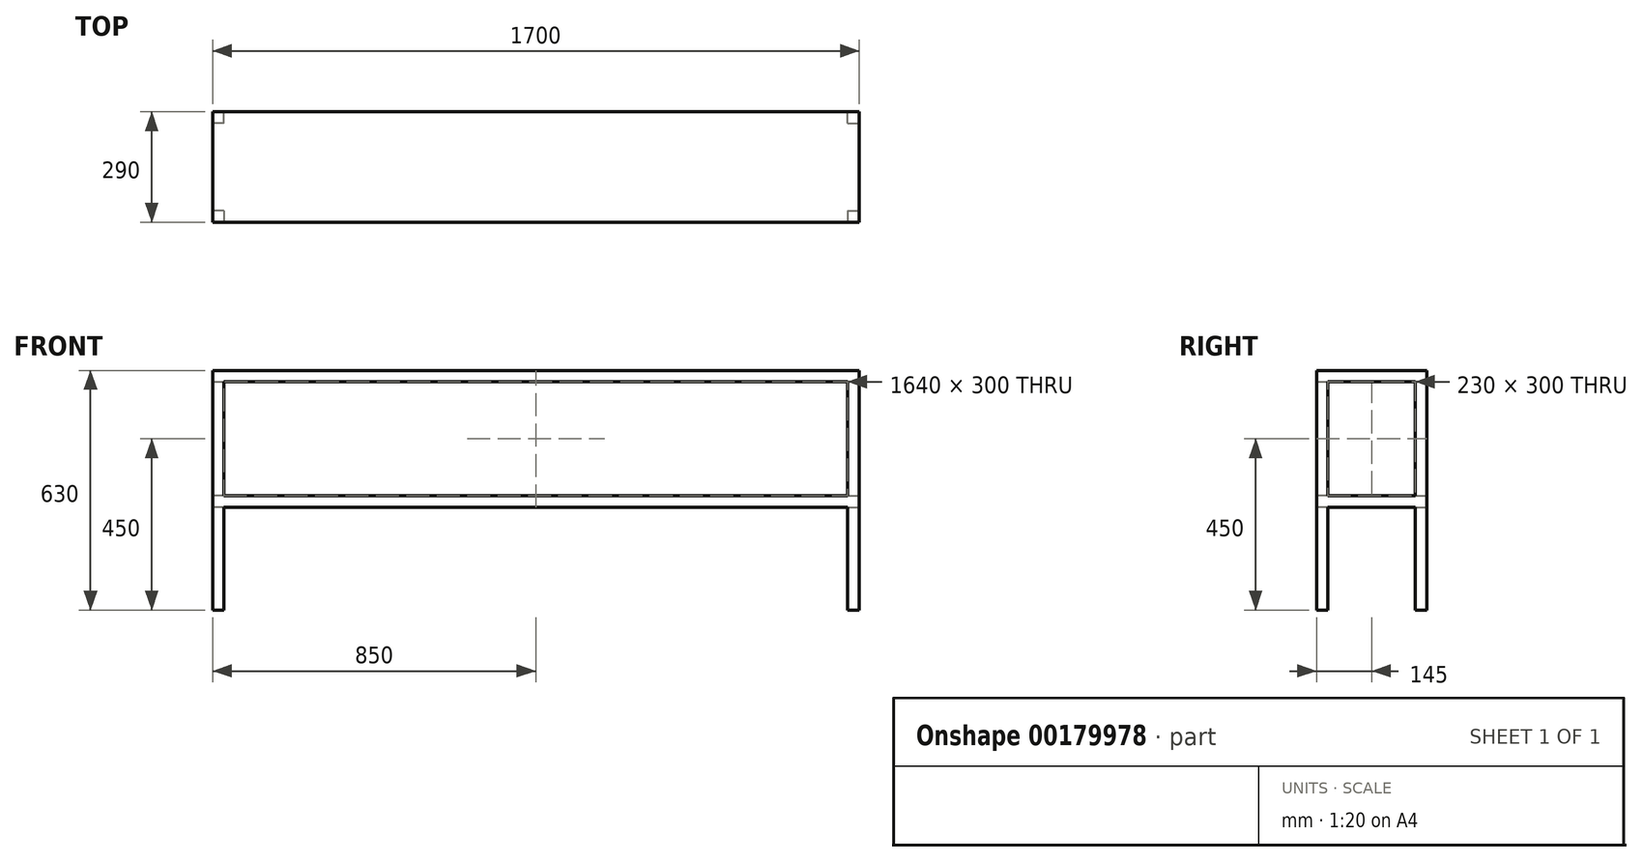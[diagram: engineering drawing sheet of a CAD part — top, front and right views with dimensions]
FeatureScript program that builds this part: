
annotation { "Feature Type Name" : "Feature", "Feature Type Description" : "" }
export const myFeature = defineFeature(function(context is Context, id is Id, definition is map)
    precondition{}
    {
        {
            var Q0;
            Q0=qCreatedBy(makeId("Top.planeOp"),FACE);
            var sketch = newSketch(context, id + "F0", { "sketchPlane" : qUnion([Q0])});
            skLineSegment(sketch, "E0.bottom", {"start": v(850, 145) * mm, "end": v(-850, 145) * mm});
            skLineSegment(sketch, "E0.top", {"start": v(850, -145) * mm, "end": v(-850, -145) * mm});
            skLineSegment(sketch, "E0.left", {"start": v(850, 145) * mm, "end": v(850, -145) * mm});
            skLineSegment(sketch, "E0.right", {"start": v(-850, 145) * mm, "end": v(-850, -145) * mm});
            skPoint(sketch, "E0.middle", {"position": v(0, 0) * mm});
            skSolve(sketch);
        }
        {
            var Q0;
            Q0 = qSketchRegion(id + "F0", true);
            extrude(context, id + "F1", {"entities" : qUnion([Q0]), "depth" : 30 * mm});
        }
        {
            var Q0;
            Q0=makeQuery(id+"F1.opExtrude","CAP_FACE",FACE,{"disambiguationData":[OSD([sQuery(id+"F0.wireOp",EDGE,"E0.bottom"),sQuery(id+"F0.wireOp",EDGE,"E0.top"),sQuery(id+"F0.wireOp",EDGE,"E0.left"),sQuery(id+"F0.wireOp",EDGE,"E0.right")])],"isStart":true});
            var sketch = newSketch(context, id + "F2", { "sketchPlane" : qUnion([Q0])});
            skLineSegment(sketch, "E1.bottom", {"start": v(-850, 145) * mm, "end": v(-820, 145) * mm});
            skLineSegment(sketch, "E1.top", {"start": v(-850, 115) * mm, "end": v(-820, 115) * mm});
            skLineSegment(sketch, "E1.left", {"start": v(-850, 145) * mm, "end": v(-850, 115) * mm});
            skLineSegment(sketch, "E1.right", {"start": v(-820, 145) * mm, "end": v(-820, 115) * mm});
            skLineSegment(sketch, "E2.bottom", {"start": v(850, 145) * mm, "end": v(820, 145) * mm});
            skLineSegment(sketch, "E2.top", {"start": v(850, 115) * mm, "end": v(820, 115) * mm});
            skLineSegment(sketch, "E2.left", {"start": v(850, 145) * mm, "end": v(850, 115) * mm});
            skLineSegment(sketch, "E2.right", {"start": v(820, 145) * mm, "end": v(820, 115) * mm});
            skLineSegment(sketch, "E3.bottom", {"start": v(850, -145) * mm, "end": v(820, -145) * mm});
            skLineSegment(sketch, "E3.top", {"start": v(850, -115) * mm, "end": v(820, -115) * mm});
            skLineSegment(sketch, "E3.left", {"start": v(850, -145) * mm, "end": v(850, -115) * mm});
            skLineSegment(sketch, "E3.right", {"start": v(820, -145) * mm, "end": v(820, -115) * mm});
            skLineSegment(sketch, "E4.bottom", {"start": v(-850, -145) * mm, "end": v(-820, -145) * mm});
            skLineSegment(sketch, "E4.top", {"start": v(-850, -115) * mm, "end": v(-820, -115) * mm});
            skLineSegment(sketch, "E4.left", {"start": v(-850, -145) * mm, "end": v(-850, -115) * mm});
            skLineSegment(sketch, "E4.right", {"start": v(-820, -145) * mm, "end": v(-820, -115) * mm});
            skSolve(sketch);
        }
        {
            var Q0;
            Q0 = qSketchRegion(id + "F2", true);
            extrude(context, id + "F3", {"entities" : qUnion([Q0]), "operationType" : NewBodyOperationType.ADD, "depth" : 600 * mm});
        }
        {
            var Q0;
            Q0=qCreatedBy(makeId("Right.planeOp"),FACE);
            var sketch = newSketch(context, id + "F4", { "sketchPlane" : qUnion([Q0])});
            skLineSegment(sketch, "E5.bottom", {"start": v(-145, -300) * mm, "end": v(145, -300) * mm});
            skLineSegment(sketch, "E5.top", {"start": v(-145, -330) * mm, "end": v(145, -330) * mm});
            skLineSegment(sketch, "E5.left", {"start": v(-145, -300) * mm, "end": v(-145, -330) * mm});
            skLineSegment(sketch, "E5.right", {"start": v(145, -300) * mm, "end": v(145, -330) * mm});
            skSolve(sketch);
        }
        {
            var Q0;
            Q0 = qSketchRegion(id + "F4", true);
            var Q1;
            Q1=makeQuery(id+"F3.boolean.opBoolean","MERGE",FACE,{"derivedFrom":[makeQuery(id+"F1.opExtrude","SWEPT_FACE",FACE,{"disambiguationData":[OSD([sQuery(id+"F0.wireOp",EDGE,"E0.left")])]}),makeQuery(id+"F3.opExtrude","SWEPT_FACE",FACE,{"disambiguationData":[OSD([sQuery(id+"F2.wireOp",EDGE,"E2.left")])]}),makeQuery(id+"F3.opExtrude","SWEPT_FACE",FACE,{"disambiguationData":[OSD([sQuery(id+"F2.wireOp",EDGE,"E3.left")])]})]});
            var Q2;
            Q2=makeQuery(id+"F3.boolean.opBoolean","MERGE",FACE,{"derivedFrom":[makeQuery(id+"F1.opExtrude","SWEPT_FACE",FACE,{"disambiguationData":[OSD([sQuery(id+"F0.wireOp",EDGE,"E0.right")])]}),makeQuery(id+"F3.opExtrude","SWEPT_FACE",FACE,{"disambiguationData":[OSD([sQuery(id+"F2.wireOp",EDGE,"E1.left")])]}),makeQuery(id+"F3.opExtrude","SWEPT_FACE",FACE,{"disambiguationData":[OSD([sQuery(id+"F2.wireOp",EDGE,"E4.left")])]})]});
            extrude(context, id + "F5", {"entities" : qUnion([Q0]), "operationType" : NewBodyOperationType.ADD, "endBound" : BoundingType.UP_TO_SURFACE, "endBoundEntityFace" : qUnion([Q1]), "depth" : 25 * mm, "hasSecondDirection" : true, "secondDirectionBound" : SecondDirectionBoundingType.UP_TO_SURFACE, "secondDirectionOppositeDirection" : true, "secondDirectionBoundEntityFace" : qUnion([Q2]), "secondDirectionDepth" : 25 * mm});
        }
    });
